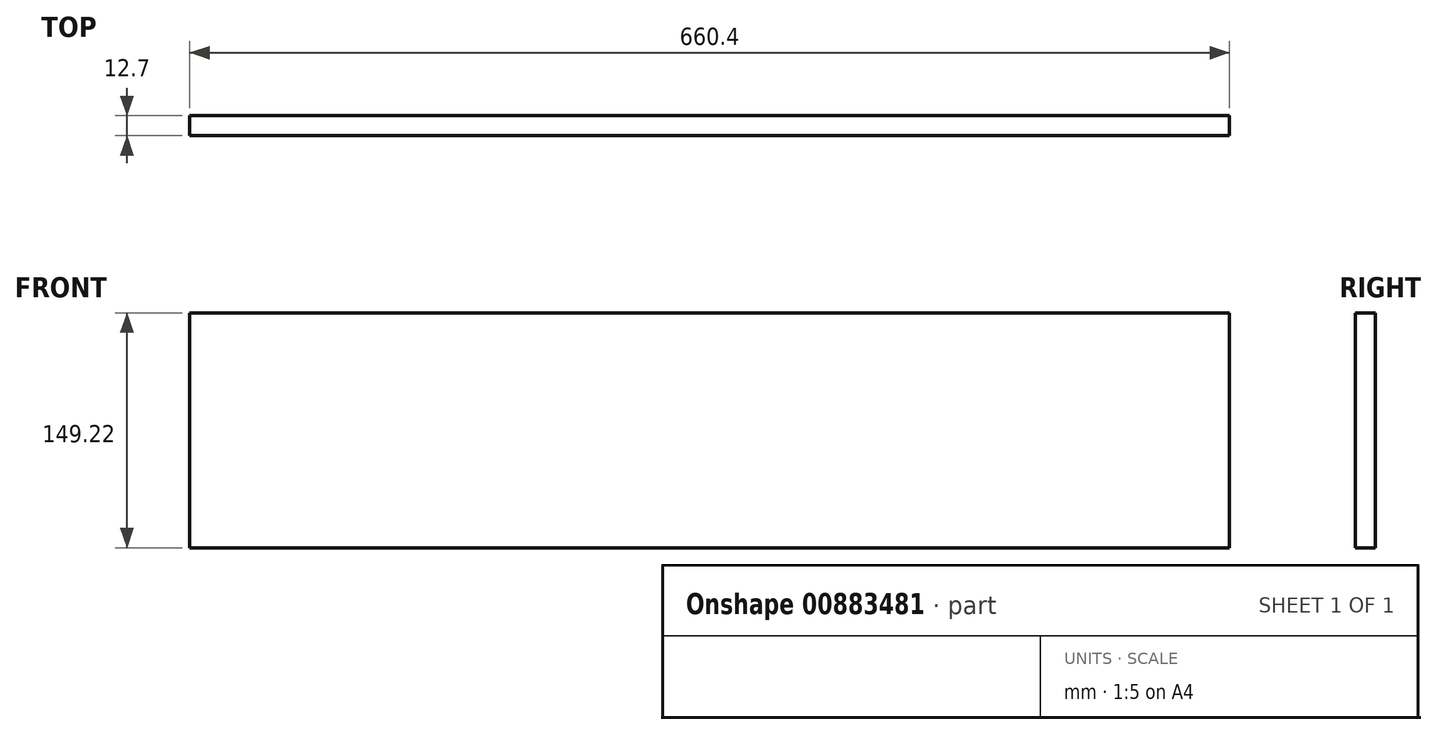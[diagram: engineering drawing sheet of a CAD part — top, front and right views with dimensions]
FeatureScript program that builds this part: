
annotation { "Feature Type Name" : "Feature", "Feature Type Description" : "" }
export const myFeature = defineFeature(function(context is Context, id is Id, definition is map)
    precondition{}
    {
        {
            var Q0;
            Q0=qCreatedBy(makeId("Front.planeOp"),FACE);
            var sketch = newSketch(context, id + "F0", { "sketchPlane" : qUnion([Q0])});
            skLineSegment(sketch, "E0.bottom", {"start": v(0, 0) * mm, "end": v(660.4, 0) * mm});
            skLineSegment(sketch, "E0.top", {"start": v(0, 149.23) * mm, "end": v(660.4, 149.23) * mm});
            skLineSegment(sketch, "E0.left", {"start": v(0, 0) * mm, "end": v(0, 149.23) * mm});
            skLineSegment(sketch, "E0.right", {"start": v(660.4, 0) * mm, "end": v(660.4, 149.23) * mm});
            skSolve(sketch);
        }
        {
            var Q0;
            Q0 = qSketchRegion(id + "F0", true);
            extrude(context, id + "F1", {"entities" : qUnion([Q0]), "depth" : 12.7 * mm, "offsetDistance" : 25.4 * mm});
        }
    });
